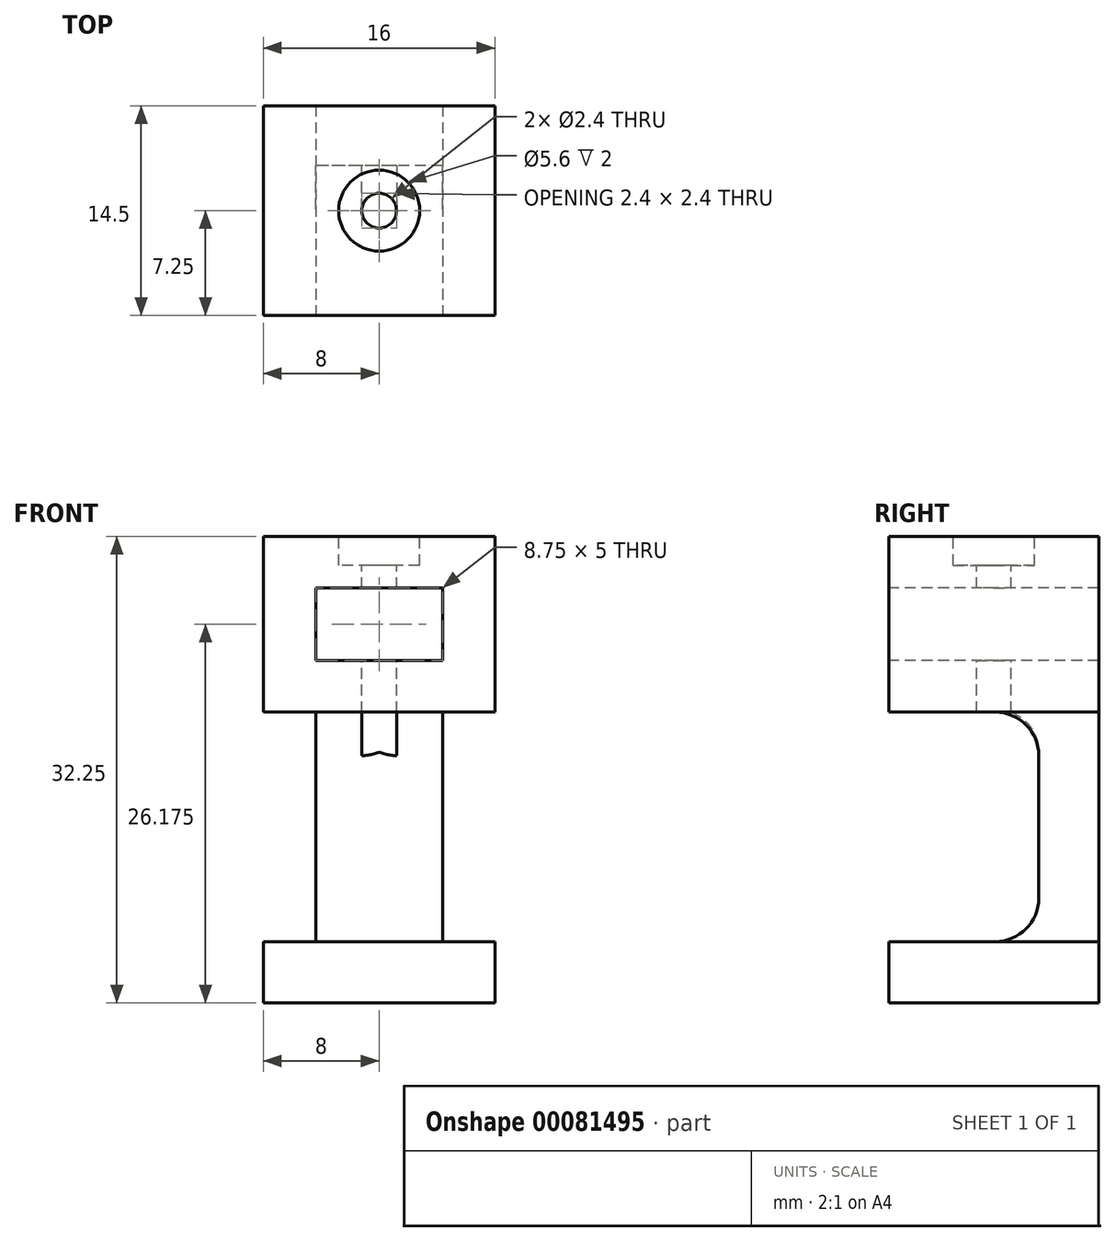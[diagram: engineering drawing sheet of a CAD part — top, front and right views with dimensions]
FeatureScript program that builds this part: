
annotation { "Feature Type Name" : "Feature", "Feature Type Description" : "" }
export const myFeature = defineFeature(function(context is Context, id is Id, definition is map)
    precondition{}
    {
        {
            var Q0;
            Q0=qCreatedBy(makeId("Top.planeOp"),FACE);
            var sketch = newSketch(context, id + "F0", { "sketchPlane" : qUnion([Q0])});
            skLineSegment(sketch, "E0.bottom", {"start": v(-8, 7.25) * mm, "end": v(8, 7.25) * mm});
            skLineSegment(sketch, "E0.top", {"start": v(-8, -7.25) * mm, "end": v(8, -7.25) * mm});
            skLineSegment(sketch, "E0.left", {"start": v(-8, 7.25) * mm, "end": v(-8, -7.25) * mm});
            skLineSegment(sketch, "E0.right", {"start": v(8, 7.25) * mm, "end": v(8, -7.25) * mm});
            skPoint(sketch, "E0.middle", {"position": v(0, 0) * mm});
            skSolve(sketch);
        }
        {
            var Q0;
            Q0 = qSketchRegion(id + "F0", true);
            extrude(context, id + "F1", {"entities" : qUnion([Q0]), "depth" : 32.25 * mm});
        }
        {
            var Q0;
            Q0=makeQuery(id+"F1.opExtrude","SWEPT_FACE",FACE,{"disambiguationData":[OSD([sQuery(id+"F0.wireOp",EDGE,"E0.top")])]});
            var sketch = newSketch(context, id + "F2", { "sketchPlane" : qUnion([Q0])});
            skLineSegment(sketch, "E1", {"start": v(-8, 20.1) * mm, "end": v(8, 20.1) * mm, "construction": true});
            skLineSegment(sketch, "E2", {"start": v(-8, 4.25) * mm, "end": v(8, 4.25) * mm, "construction": true});
            skLineSegment(sketch, "E3", {"start": v(-4.38, 20.1) * mm, "end": v(-4.38, 4.25) * mm});
            skLineSegment(sketch, "E4", {"start": v(4.37, 20.1) * mm, "end": v(4.37, 4.25) * mm});
            skLineSegment(sketch, "E5", {"start": v(-8, 4.25) * mm, "end": v(8, 4.25) * mm});
            skLineSegment(sketch, "E6", {"start": v(-8, 20.1) * mm, "end": v(-4.38, 20.1) * mm});
            skLineSegment(sketch, "E7", {"start": v(4.37, 20.1) * mm, "end": v(8, 20.1) * mm});
            skSolve(sketch);
        }
        {
            var Q0;
            {var subQ0=sQuery(id+"F2.wireOp",EDGE,"E3");Q0=makeQuery(id+"F2.imprint","IMPRINT",FACE,{"disambiguationData":[TD([[makeQuery(id+"F2.imprint","IMPRINT",EDGE,{"derivedFrom":subQ0}),-1.0]])]});}
            var Q1;
            {var subQ0=sQuery(id+"F2.wireOp",EDGE,"E4");Q1=makeQuery(id+"F2.imprint","IMPRINT",FACE,{"disambiguationData":[TD([[makeQuery(id+"F2.imprint","IMPRINT",EDGE,{"derivedFrom":subQ0}),1.0]])]});}
            extrude(context, id + "F3", {"entities" : qUnion([Q0, Q1]), "operationType" : NewBodyOperationType.REMOVE, "oppositeDirection" : true, "depth" : 15.25 * mm});
        }
        {
            var Q0;
            Q0=makeQuery(id+"F3.boolean.opBoolean","COPY",FACE,{"derivedFrom":makeQuery(id+"F3.opExtrude","SWEPT_FACE",FACE,{"disambiguationData":[OSD([sQuery(id+"F2.wireOp",EDGE,"E3")])]})});
            var sketch = newSketch(context, id + "F4", { "sketchPlane" : qUnion([Q0])});
            skLineSegment(sketch, "E8.bottom", {"start": v(7.25, 20.1) * mm, "end": v(-3.1, 20.1) * mm});
            skLineSegment(sketch, "E8.top", {"start": v(7.25, 4.25) * mm, "end": v(-3.1, 4.25) * mm});
            skLineSegment(sketch, "E8.left", {"start": v(7.25, 20.1) * mm, "end": v(7.25, 4.25) * mm});
            skLineSegment(sketch, "E8.right", {"start": v(-3.1, 20.1) * mm, "end": v(-3.1, 4.25) * mm});
            skSolve(sketch);
        }
        {
            var Q0;
            Q0=makeQuery(id+"F4.imprint","IMPRINT",FACE,{"disambiguationData":[TD([[makeQuery(id+"F4.imprint","IMPRINT",EDGE,{"derivedFrom":sQuery(id+"F4.wireOp",EDGE,"E8.bottom")}),-1.0]])]});
            extrude(context, id + "F5", {"entities" : qUnion([Q0]), "operationType" : NewBodyOperationType.REMOVE, "oppositeDirection" : true, "depth" : 16 * mm});
        }
        {
            var Q0;
            {var subQ2=sQuery(id+"F0.wireOp",EDGE,"E0.top");Q0=makeQuery(id+"F5.boolean.opBoolean","SPLIT",FACE,{"disambiguationData":[TD([makeQuery(id+"F3.boolean.opBoolean","COPY",FACE,{"derivedFrom":makeQuery(id+"F3.opExtrude","SWEPT_FACE",FACE,{"disambiguationData":[OSD([sQuery(id+"F2.wireOp",EDGE,"E6")])]})})])],"derivedFrom":makeQuery(id+"F1.opExtrude","SWEPT_FACE",FACE,{"disambiguationData":[OSD([subQ2])]})});}
            var sketch = newSketch(context, id + "F6", { "sketchPlane" : qUnion([Q0])});
            skLineSegment(sketch, "E9", {"start": v(-8, 20.1) * mm, "end": v(8, 32.25) * mm, "construction": true});
            skLineSegment(sketch, "E10", {"start": v(-8, 32.25) * mm, "end": v(8, 20.1) * mm, "construction": true});
            skPoint(sketch, "E11", {"position": v(0, 26.18) * mm});
            skLineSegment(sketch, "E12.bottom", {"start": v(-4.38, 28.67) * mm, "end": v(4.37, 28.67) * mm});
            skLineSegment(sketch, "E12.top", {"start": v(-4.38, 23.67) * mm, "end": v(4.37, 23.67) * mm});
            skLineSegment(sketch, "E12.left", {"start": v(-4.38, 28.67) * mm, "end": v(-4.38, 23.67) * mm});
            skLineSegment(sketch, "E12.right", {"start": v(4.37, 28.67) * mm, "end": v(4.37, 23.67) * mm});
            skSolve(sketch);
        }
        {
            var Q0;
            Q0=makeQuery(id+"F6.imprint","IMPRINT",FACE,{"disambiguationData":[TD([[makeQuery(id+"F6.imprint","IMPRINT",EDGE,{"derivedFrom":sQuery(id+"F6.wireOp",EDGE,"E12.bottom")}),-1.0]])]});
            extrude(context, id + "F7", {"entities" : qUnion([Q0]), "operationType" : NewBodyOperationType.REMOVE, "oppositeDirection" : true, "depth" : 14.5 * mm});
        }
        {
            var Q0;
            Q0=makeQuery(id+"F1.opExtrude","CAP_FACE",FACE,{"disambiguationData":[OSD([sQuery(id+"F0.wireOp",EDGE,"E0.bottom"),sQuery(id+"F0.wireOp",EDGE,"E0.top"),sQuery(id+"F0.wireOp",EDGE,"E0.left"),sQuery(id+"F0.wireOp",EDGE,"E0.right")])],"isStart":false});
            var sketch = newSketch(context, id + "F8", { "sketchPlane" : qUnion([Q0])});
            skCircle(sketch, "E13", {"center": v(0, 0) * mm, "radius": 2.8 * mm});
            skCircle(sketch, "E14", {"center": v(0, 0) * mm, "radius": 1.2 * mm});
            skSolve(sketch);
        }
        {
            var Q0;
            Q0=makeQuery(id+"F8.imprint","IMPRINT",FACE,{"disambiguationData":[TD([[makeQuery(id+"F8.imprint","IMPRINT",EDGE,{"derivedFrom":sQuery(id+"F8.wireOp",EDGE,"E13")}),1.0]])]});
            extrude(context, id + "F9", {"entities" : qUnion([Q0]), "operationType" : NewBodyOperationType.REMOVE, "oppositeDirection" : true, "depth" : 2 * mm});
        }
        {
            var Q0;
            Q0=makeQuery(id+"F9.boolean.opBoolean","SPLIT",FACE,{"disambiguationData":[TD([makeQuery(id+"F9.opExtrude","SWEPT_FACE",FACE,{"disambiguationData":[OSD([sQuery(id+"F8.wireOp",EDGE,"E14")])]})])],"derivedFrom":makeQuery(id+"F1.opExtrude","CAP_FACE",FACE,{"disambiguationData":[OSD([sQuery(id+"F0.wireOp",EDGE,"E0.bottom"),sQuery(id+"F0.wireOp",EDGE,"E0.top"),sQuery(id+"F0.wireOp",EDGE,"E0.left"),sQuery(id+"F0.wireOp",EDGE,"E0.right")])],"isStart":false})});
            extrude(context, id + "F10", {"entities" : qUnion([Q0]), "operationType" : NewBodyOperationType.REMOVE, "oppositeDirection" : true, "depth" : 12.5 * mm});
        }
        {
            var Q0;
            Q0=makeQuery(id+"F5.boolean.opBoolean","COPY",EDGE,{"derivedFrom":makeQuery(id+"F5.opExtrude","SWEPT_EDGE",EDGE,{"disambiguationData":[OSD([sQuery(id+"F2.wireOp",EDGE,"E3"),sQuery(id+"F2.wireOp",EDGE,"E5"),sQuery(id+"F4.wireOp",EDGE,"E8.top"),sQuery(id+"F4.wireOp",EDGE,"E8.right")])]})});
            var Q1;
            Q1=makeQuery(id+"F5.boolean.opBoolean","COPY",EDGE,{"derivedFrom":makeQuery(id+"F5.opExtrude","SWEPT_EDGE",EDGE,{"disambiguationData":[OSD([sQuery(id+"F2.wireOp",EDGE,"E3"),sQuery(id+"F2.wireOp",EDGE,"E6"),sQuery(id+"F4.wireOp",EDGE,"E8.bottom"),sQuery(id+"F4.wireOp",EDGE,"E8.right")])]})});
            fillet(context, id + "F11", {"entities" : qUnion([Q0, Q1]), "radius" : 3 * mm, "tangentPropagation" : true, "allowEdgeOverflow" : false});
        }
    });
